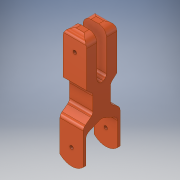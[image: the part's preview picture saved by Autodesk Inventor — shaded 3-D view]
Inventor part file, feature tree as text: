
AUTODESK INVENTOR PART (.ipt)
format: ipt  version: 2017 (Build 210142000, 142)  size: 210,432 bytes
history: native  units: in
note: dims shown in document units (in); Inventor stores cm internally (conversion verified against a paired STEP export)
features: sketch x4, extrude x4, fillet x4, plane x2, mirror x1
ambient origin geometry x8: Origin, YZ Plane, XZ Plane, XY Plane, X Axis, Y Axis, Z Axis, Center Point
bodies: Solid1 (feature_tree)
feature tree (15):
  sketch  "Sketch1"  dims[d3=0.2165in d6=0.7087in]
  plane  "Work Plane1"
  extrude  "Extrusion1"  Depth=0.7087in
  extrude  "Extrusion2"  Depth=0.5315in
  extrude  "Extrusion3"  Depth=1.4173in TaperAngle=0.0deg
  plane  "Work Plane3"
  mirror  "Mirror1"
  sketch  "Sketch6"  dims[d66=1.1811in d67=0.0in d72=0.315in d73=0.315in d74=0.315in d75=0.315in d76=0.315in d77=1.8504in d78=0.0in]
  fillet  "Fillet1"  Radius=0.1575in
  fillet  "Fillet2"  Radius=4.9213in
  fillet  "Fillet3"  [1 undecoded]
  fillet  "Fillet4"  Radius=0.2165in
  extrude  "Extrusion4"  Depth=0.315in
  sketch  "Sketch3"  dims[d7=1.9882in d53=0.5315in]
  sketch  "Sketch5"  dims[d56=0.6299in d58=1.4173in d59=0.0in d60=0.1575in d61=0.0in d63=4.9213in d64=0.0in d65=0.2165in]
note: 1 required parameter value undecoded (feature->parameter linkage not recoverable at this tier; creation-order binding heuristic only, values carry confidence <= 0.55)
